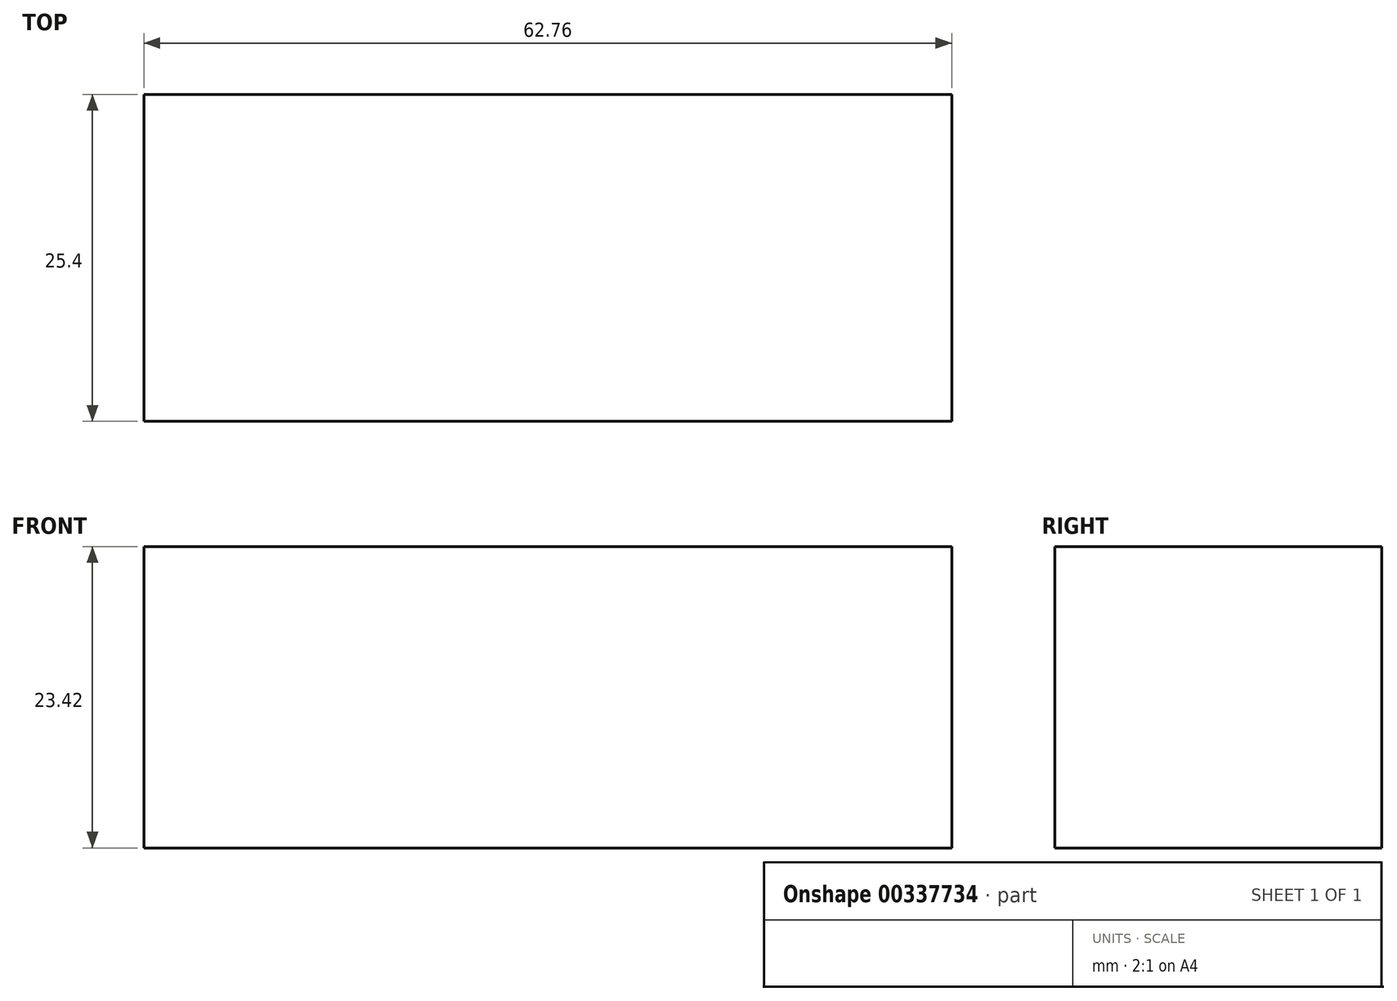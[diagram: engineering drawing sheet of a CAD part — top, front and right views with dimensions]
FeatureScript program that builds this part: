
annotation { "Feature Type Name" : "Feature", "Feature Type Description" : "" }
export const myFeature = defineFeature(function(context is Context, id is Id, definition is map)
    precondition{}
    {
        {
            var Q0;
            Q0=qCreatedBy(makeId("Front.planeOp"),FACE);
            var sketch = newSketch(context, id + "F0", { "sketchPlane" : qUnion([Q0])});
            skLineSegment(sketch, "E0", {"start": v(-63.72, 71.2) * mm, "end": v(-63.72, -53.37) * mm});
            skLineSegment(sketch, "E1", {"start": v(-63.72, -53.37) * mm, "end": v(32.58, 47.5) * mm});
            skLineSegment(sketch, "E2.bottom", {"start": v(-30.18, 58.12) * mm, "end": v(32.58, 58.12) * mm});
            skLineSegment(sketch, "E2.top", {"start": v(-30.18, 81.54) * mm, "end": v(32.58, 81.54) * mm});
            skLineSegment(sketch, "E2.left", {"start": v(-30.18, 58.12) * mm, "end": v(-30.18, 81.54) * mm});
            skLineSegment(sketch, "E2.right", {"start": v(32.58, 58.12) * mm, "end": v(32.58, 81.54) * mm});
            skSolve(sketch);
        }
        {
            var Q0;
            Q0=makeQuery(id+"F0.imprint","IMPRINT",FACE,{"disambiguationData":[TD([[makeQuery(id+"F0.imprint","IMPRINT",EDGE,{"derivedFrom":sQuery(id+"F0.wireOp",EDGE,"E2.bottom")}),1.0]])]});
            var Q1;
            Q1 = qSketchRegion(id + "F0", true);
            extrude(context, id + "F1", {"entities" : qUnion([Q0, Q1]), "depth" : 25.4 * mm});
        }
    });
